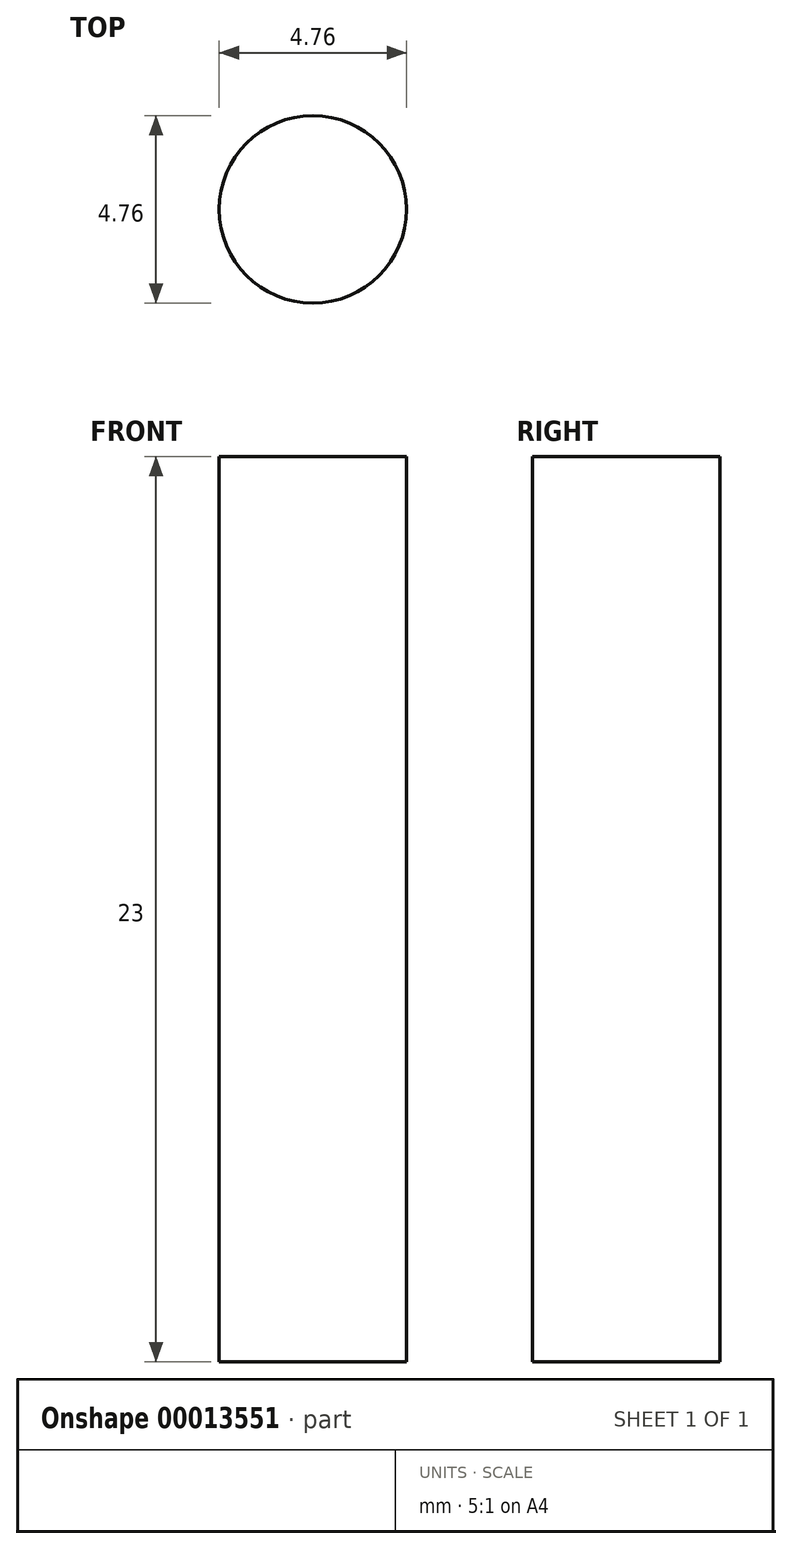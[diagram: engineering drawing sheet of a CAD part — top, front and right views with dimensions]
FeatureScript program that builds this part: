
annotation { "Feature Type Name" : "Feature", "Feature Type Description" : "" }
export const myFeature = defineFeature(function(context is Context, id is Id, definition is map)
    precondition{}
    {
        {
            var Q0;
            Q0=qCreatedBy(makeId("Top.planeOp"),FACE);
            var sketch = newSketch(context, id + "F0", { "sketchPlane" : qUnion([Q0])});
            skCircle(sketch, "E0", {"center": v(0, 0) * mm, "radius": 2.38 * mm});
            skSolve(sketch);
        }
        {
            var Q0;
            Q0 = qSketchRegion(id + "F0", true);
            extrude(context, id + "F1", {"entities" : qUnion([Q0]), "depth" : 23 * mm});
        }
    });
